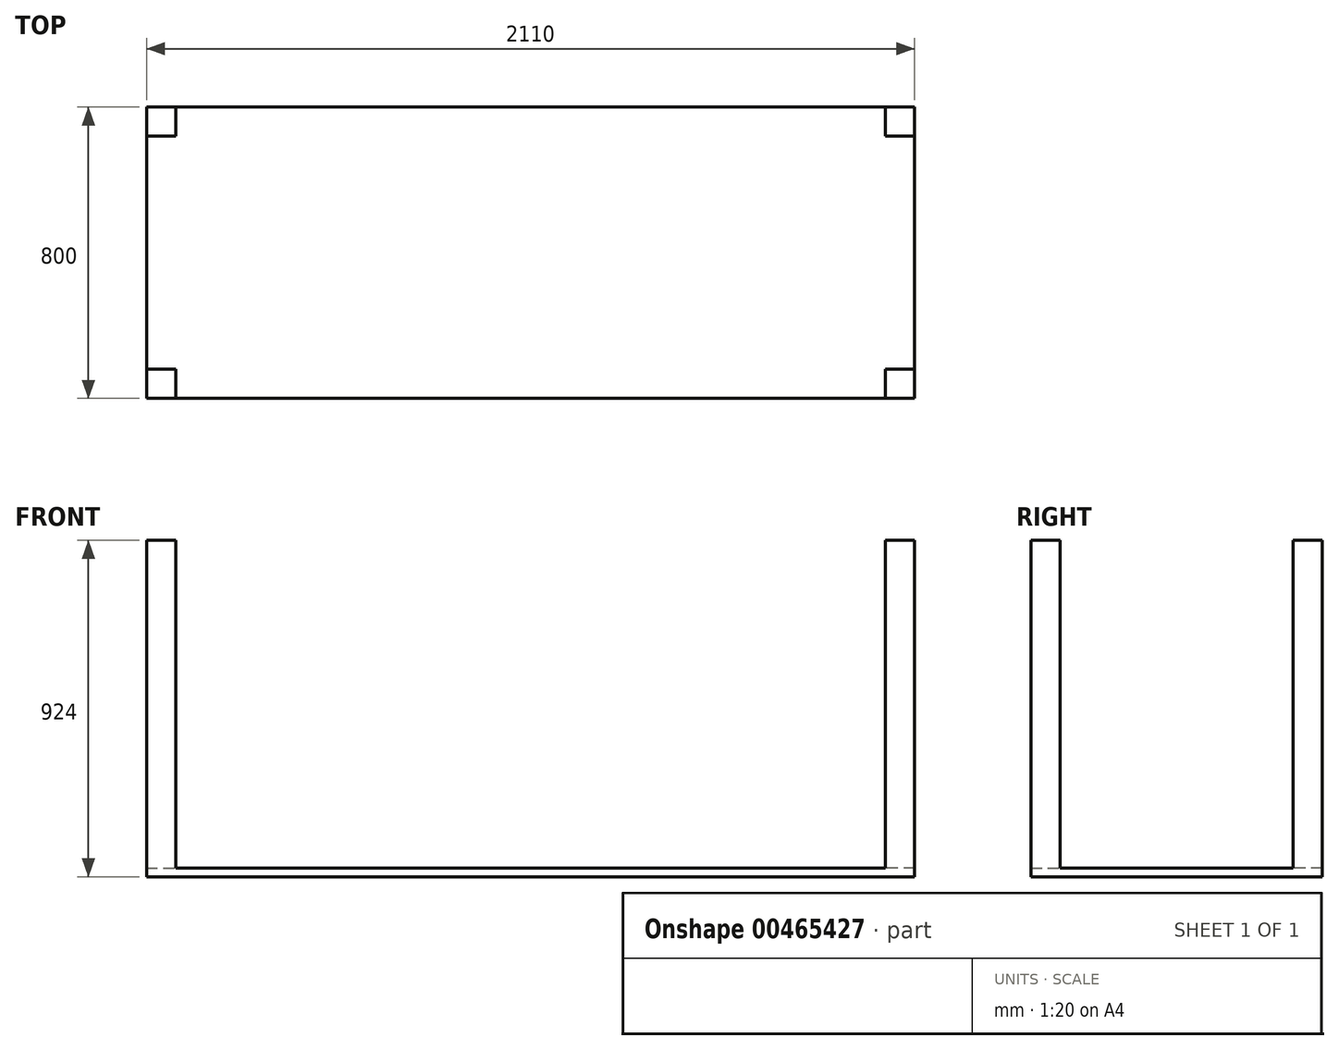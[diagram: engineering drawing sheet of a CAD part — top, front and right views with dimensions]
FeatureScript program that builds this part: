
annotation { "Feature Type Name" : "Feature", "Feature Type Description" : "" }
export const myFeature = defineFeature(function(context is Context, id is Id, definition is map)
    precondition{}
    {
        {
            var Q0;
            Q0=qCreatedBy(makeId("Top.planeOp"),FACE);
            var sketch = newSketch(context, id + "F0", { "sketchPlane" : qUnion([Q0])});
            skLineSegment(sketch, "E0.bottom", {"start": v(-803.9, 834.22) * mm, "end": v(1306.1, 834.22) * mm});
            skLineSegment(sketch, "E0.top", {"start": v(-803.9, 34.22) * mm, "end": v(1306.1, 34.22) * mm});
            skLineSegment(sketch, "E0.left", {"start": v(-803.9, 834.22) * mm, "end": v(-803.9, 34.22) * mm});
            skLineSegment(sketch, "E0.right", {"start": v(1306.1, 834.22) * mm, "end": v(1306.1, 34.22) * mm});
            skSolve(sketch);
        }
        {
            var Q0;
            Q0 = qSketchRegion(id + "F0", true);
            extrude(context, id + "F1", {"entities" : qUnion([Q0]), "depth" : 24 * mm, "offsetDistance" : 25 * mm});
        }
        {
            var Q0;
            Q0=makeQuery(id+"F1.opExtrude","CAP_FACE",FACE,{"disambiguationData":[OSD([sQuery(id+"F0.wireOp",EDGE,"E0.bottom"),sQuery(id+"F0.wireOp",EDGE,"E0.top"),sQuery(id+"F0.wireOp",EDGE,"E0.left"),sQuery(id+"F0.wireOp",EDGE,"E0.right")])],"isStart":false});
            var sketch = newSketch(context, id + "F2", { "sketchPlane" : qUnion([Q0])});
            skLineSegment(sketch, "E1.bottom", {"start": v(-803.9, 34.22) * mm, "end": v(-723.9, 34.22) * mm});
            skLineSegment(sketch, "E1.top", {"start": v(-803.9, 114.22) * mm, "end": v(-723.9, 114.22) * mm});
            skLineSegment(sketch, "E1.left", {"start": v(-803.9, 34.22) * mm, "end": v(-803.9, 114.22) * mm});
            skLineSegment(sketch, "E1.right", {"start": v(-723.9, 34.22) * mm, "end": v(-723.9, 114.22) * mm});
            skLineSegment(sketch, "E2.bottom", {"start": v(-803.9, 834.22) * mm, "end": v(-723.9, 834.22) * mm});
            skLineSegment(sketch, "E2.top", {"start": v(-803.9, 754.22) * mm, "end": v(-723.9, 754.22) * mm});
            skLineSegment(sketch, "E2.left", {"start": v(-803.9, 834.22) * mm, "end": v(-803.9, 754.22) * mm});
            skLineSegment(sketch, "E2.right", {"start": v(-723.9, 834.22) * mm, "end": v(-723.9, 754.22) * mm});
            skLineSegment(sketch, "E3.bottom", {"start": v(1306.1, 834.22) * mm, "end": v(1226.1, 834.22) * mm});
            skLineSegment(sketch, "E3.top", {"start": v(1306.1, 754.22) * mm, "end": v(1226.1, 754.22) * mm});
            skLineSegment(sketch, "E3.left", {"start": v(1306.1, 834.22) * mm, "end": v(1306.1, 754.22) * mm});
            skLineSegment(sketch, "E3.right", {"start": v(1226.1, 834.22) * mm, "end": v(1226.1, 754.22) * mm});
            skLineSegment(sketch, "E4.bottom", {"start": v(1306.1, 34.22) * mm, "end": v(1226.1, 34.22) * mm});
            skLineSegment(sketch, "E4.top", {"start": v(1306.1, 114.22) * mm, "end": v(1226.1, 114.22) * mm});
            skLineSegment(sketch, "E4.left", {"start": v(1306.1, 34.22) * mm, "end": v(1306.1, 114.22) * mm});
            skLineSegment(sketch, "E4.right", {"start": v(1226.1, 34.22) * mm, "end": v(1226.1, 114.22) * mm});
            skSolve(sketch);
        }
        {
            var Q0;
            Q0 = qSketchRegion(id + "F2", true);
            extrude(context, id + "F3", {"entities" : qUnion([Q0]), "operationType" : NewBodyOperationType.ADD, "depth" : 900 * mm, "offsetDistance" : 25 * mm});
        }
    });
